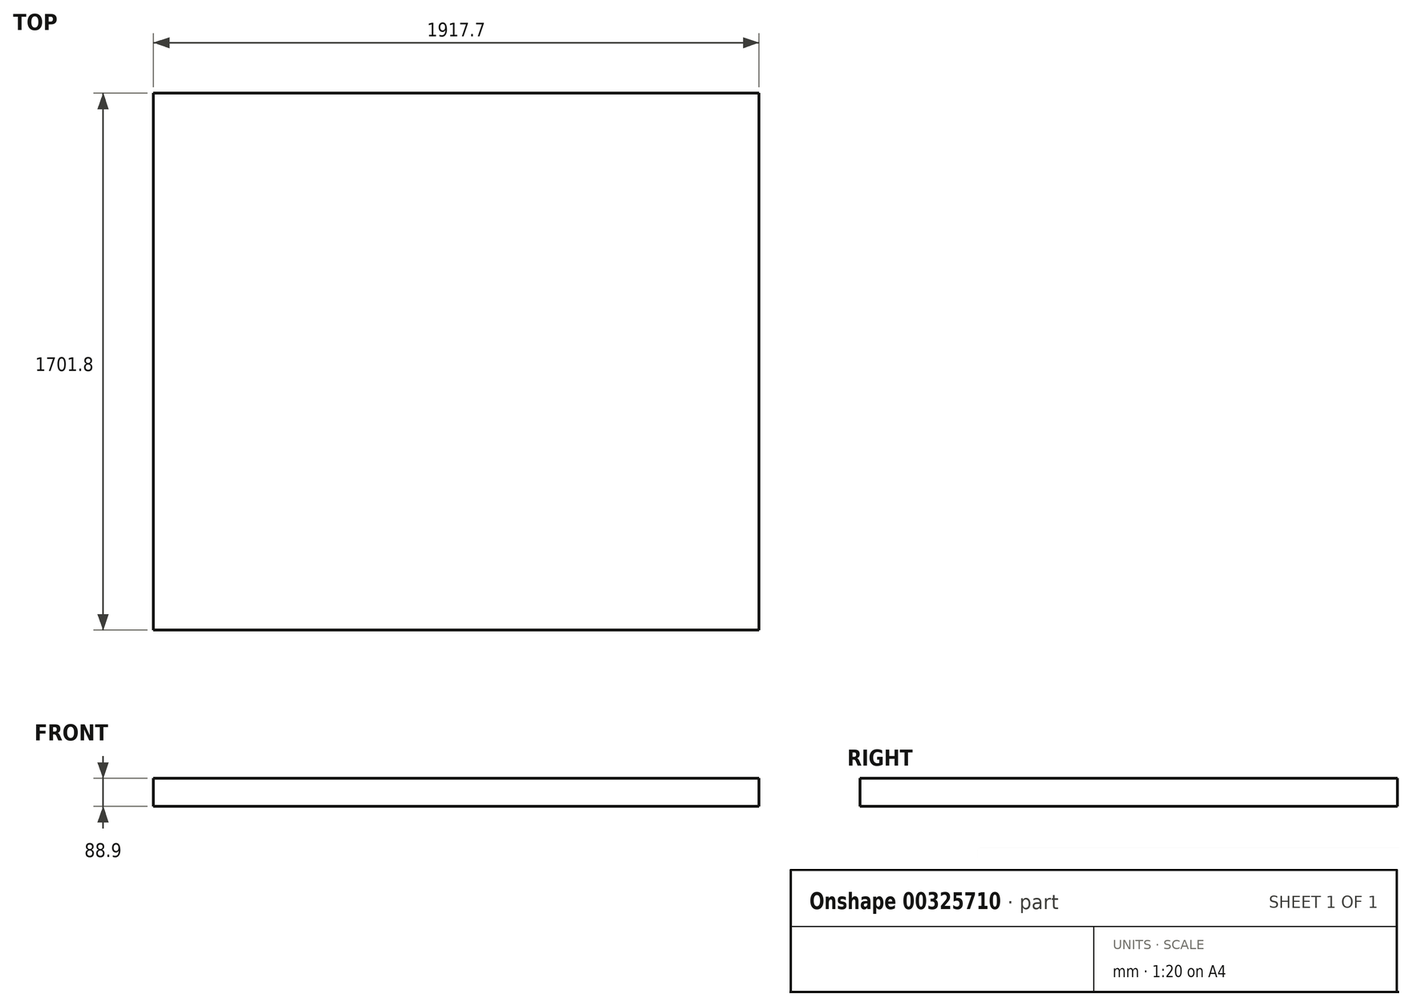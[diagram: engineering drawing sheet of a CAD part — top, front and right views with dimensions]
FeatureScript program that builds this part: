
annotation { "Feature Type Name" : "Feature", "Feature Type Description" : "" }
export const myFeature = defineFeature(function(context is Context, id is Id, definition is map)
    precondition{}
    {
        {
            var Q0;
            Q0=qCreatedBy(makeId("Top.planeOp"),FACE);
            var sketch = newSketch(context, id + "F0", { "sketchPlane" : qUnion([Q0])});
            skLineSegment(sketch, "E0.bottom", {"start": v(-66.74, 1635.36) * mm, "end": v(1850.96, 1635.36) * mm});
            skLineSegment(sketch, "E0.top", {"start": v(-66.74, -66.44) * mm, "end": v(1850.96, -66.44) * mm});
            skLineSegment(sketch, "E0.left", {"start": v(-66.74, 1635.36) * mm, "end": v(-66.74, -66.44) * mm});
            skLineSegment(sketch, "E0.right", {"start": v(1850.96, 1635.36) * mm, "end": v(1850.96, -66.44) * mm});
            skSolve(sketch);
        }
        {
            var Q0;
            Q0=makeQuery(id+"F0.imprint","IMPRINT",FACE,{"disambiguationData":[TD([[makeQuery(id+"F0.imprint","IMPRINT",EDGE,{"derivedFrom":sQuery(id+"F0.wireOp",EDGE,"E0.bottom")}),-1.0]])]});
            var Q1;
            Q1=sQuery(id+"F0.wireOp",EDGE,"E0.top");
            extrude(context, id + "F1", {"entities" : qUnion([Q0]), "surfaceEntities" : qUnion([Q1]), "endBound" : BoundingType.SYMMETRIC, "depth" : 88.9 * mm, "hasSecondDirection" : true, "secondDirectionBound" : SecondDirectionBoundingType.UP_TO_NEXT, "secondDirectionOppositeDirection" : true, "secondDirectionDepth" : 25.4 * mm});
        }
    });
